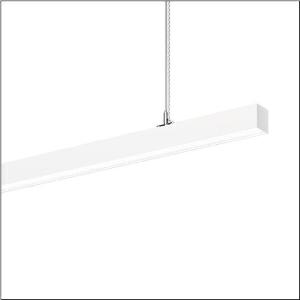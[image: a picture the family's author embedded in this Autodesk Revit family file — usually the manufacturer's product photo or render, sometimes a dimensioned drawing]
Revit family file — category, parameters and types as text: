
# Revit family: silica_r__21_51mx30tct9w_581c
name_source: partatom
category: Lighting Fixtures
units: mm (PartAtom-declared; Revit-internal decimal feet)

## family parameters
Cut with Voids When Loaded = No
Host = Face
Light Source = No
Part Type = Normal
Room Calculation Point = No
Round Connector Dimension = Use Diameter
Shared = No

## types (1)
- --- (1 x LED, 10300 lm, 84.4 W, 6500K)
    Apparent Load = 84 VA
    CIE Flux Codes = 47 79 96 58 100
    Color Rendering = 80
    Color Temperature = 6500K
    Default Elevation = 1800 mm
    Description = Silica® 21, office luminaire, primary optical cover: cover, of PMMA, opal, light emission: direct/indirect distribution, primary light characteristic: symmetric, installation type: suspended mounting, LED, rated luminous flux: 10.300lm, luminous efficacy: 116lm/W, light colour: 8tw, colour temperature: 2700..6500K, control gear: ECG DALI, with terminal, 3+2-pole, max. 2.5mm², mains connection: 220..240V, AC, 50/60Hz, rated input power: 88.7W, luminaire housing, of aluminium, traffic white (RAL 9016), length: 3.004mm, width: 53mm, height: 53mm, protection rating (complete): IP20, insulation class (complete): insulation class I (protective earthing), certification: CE, permissible operating ambient temperature: 0..+35°C, standard: EN 50419, packaging unit: 1 piece
    Height = 53 mm
    Lamp = 1 x LED
    Lamp Light Flux = 10300 lm
    Lamp Power = 84.4 W
    Lamp count = 1
    Length = 3004 mm
    Luminous efficacy = 122 lm/W
    Manufacturer = Siteco
    ModVariant = No
    Model = 51MX30TCT9W
    Mounting Place = Ceiling
    Mounting Type = Pendant
    Number of Poles = 1
    OnlyDefault = Yes
    Power Factor = 1
    Product Name = Silica® 21
    Product group = office luminaire | ceiling pendant
    ProductGroupID = 902
    Protection Class = Protection class I
    Protection Degree = IP 20
    RLX_Detail_Level = 1
    RLX_Emergency_Light_Flux = 0 lm
    RLX_Emergency_Type = 0
    RLX_Emergency_Type_DB = No
    RlxData = <blob elided: 18013 chars, md5=a4b583bf>
    Socket = socket
    Standby Power = 0 W
    System Light Flux = 10300 lm
    System Power = 84 W
    Type Comments = individual setting
    Type Image = l_1297784.jpg
    URL = http://relux.com
    VarID = @adj_070969
    Voltage = 0 V
    Weight = 0.00 kg
    Width = 53 mm

## geometry (parser evidence)
native form markers: Blend x4, Sweep x13
no freeform markers — native parametric forms only
